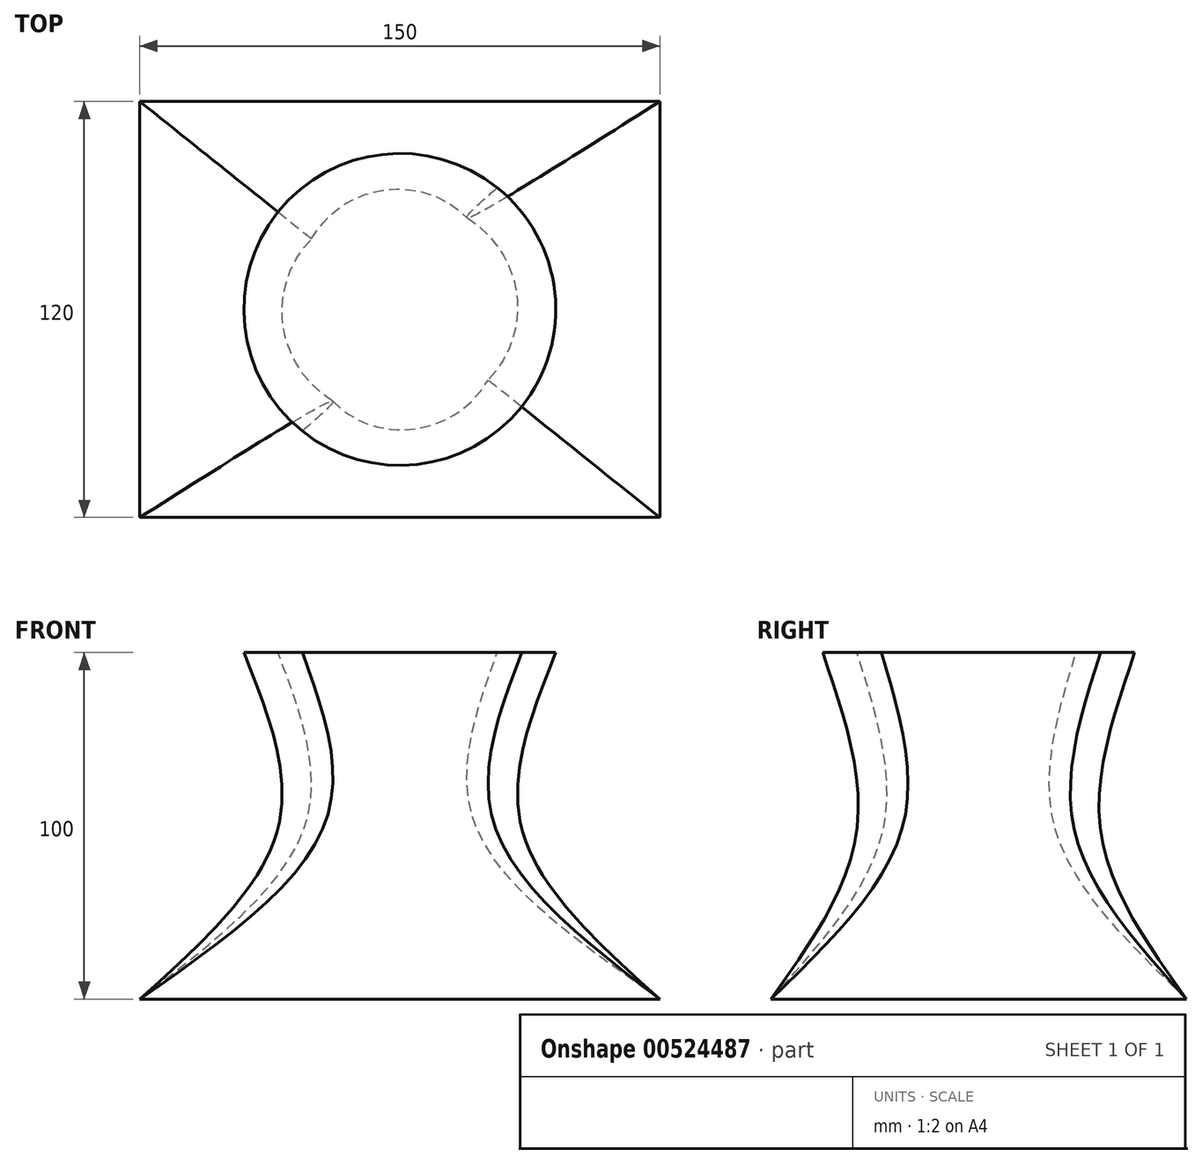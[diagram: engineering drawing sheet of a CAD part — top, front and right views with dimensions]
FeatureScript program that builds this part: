
annotation { "Feature Type Name" : "Feature", "Feature Type Description" : "" }
export const myFeature = defineFeature(function(context is Context, id is Id, definition is map)
    precondition{}
    {
        {
            var Q0;
            Q0=qCreatedBy(makeId("Top.planeOp"),FACE);
            var sketch = newSketch(context, id + "F0", { "sketchPlane" : qUnion([Q0])});
            skLineSegment(sketch, "E0.bottom", {"start": v(75, -60) * mm, "end": v(-75, -60) * mm});
            skLineSegment(sketch, "E0.top", {"start": v(75, 60) * mm, "end": v(-75, 60) * mm});
            skLineSegment(sketch, "E0.left", {"start": v(75, -60) * mm, "end": v(75, 60) * mm});
            skLineSegment(sketch, "E0.right", {"start": v(-75, -60) * mm, "end": v(-75, 60) * mm});
            skPoint(sketch, "E0.middle", {"position": v(0, 0) * mm});
            skSolve(sketch);
        }
        {
            var Q0;
            Q0=qCreatedBy(makeId("Top.planeOp"),FACE);
            cPlane(context, id + "F1", {"entities" : qUnion([Q0]), "cplaneType" : CPlaneType.OFFSET, "offset" : 100 * mm, "width" : 150 * mm, "height" : 150 * mm});
        }
        {
            var Q0;
            Q0=qCreatedBy(makeId("Top.planeOp"),FACE);
            var Q1;
            Q1=qCreatedBy(id+"F1.planeOp",FACE);
            cPlane(context, id + "F2", {"entities" : qUnion([Q0, Q1]), "cplaneType" : CPlaneType.MID_PLANE, "offset" : 25 * mm, "width" : 150 * mm, "height" : 150 * mm});
        }
        {
            var Q0;
            Q0=qCreatedBy(id+"F1.planeOp",FACE);
            var sketch = newSketch(context, id + "F3", { "sketchPlane" : qUnion([Q0])});
            skCircle(sketch, "E1", {"center": v(0, 0) * mm, "radius": 45 * mm});
            skSolve(sketch);
        }
        {
            var Q0;
            Q0=qCreatedBy(id+"F2.planeOp",FACE);
            var sketch = newSketch(context, id + "F4", { "sketchPlane" : qUnion([Q0])});
            skCircle(sketch, "E2", {"center": v(0, 0) * mm, "radius": 35 * mm});
            skSolve(sketch);
        }
        {
            var Q0;
            Q0=makeQuery(id+"F0.imprint","IMPRINT",FACE,{"disambiguationData":[TD([[makeQuery(id+"F0.imprint","IMPRINT",EDGE,{"derivedFrom":sQuery(id+"F0.wireOp",EDGE,"E0.bottom")}),-1.0]])]});
            var Q1;
            Q1=makeQuery(id+"F4.imprint","IMPRINT",FACE,{"disambiguationData":[TD([[makeQuery(id+"F4.imprint","IMPRINT",EDGE,{"derivedFrom":sQuery(id+"F4.wireOp",EDGE,"E2")}),1.0]])]});
            var Q2;
            Q2=makeQuery(id+"F3.imprint","IMPRINT",FACE,{"disambiguationData":[TD([[makeQuery(id+"F3.imprint","IMPRINT",EDGE,{"derivedFrom":sQuery(id+"F3.wireOp",EDGE,"E1")}),1.0]])]});
            loft(context, id + "F5", {"sheetProfilesArray" : [{ "sheetProfileEntities" : qUnion([Q0]) }, { "sheetProfileEntities" : qUnion([Q1]) }, { "sheetProfileEntities" : qUnion([Q2]) }]});
        }
    });
